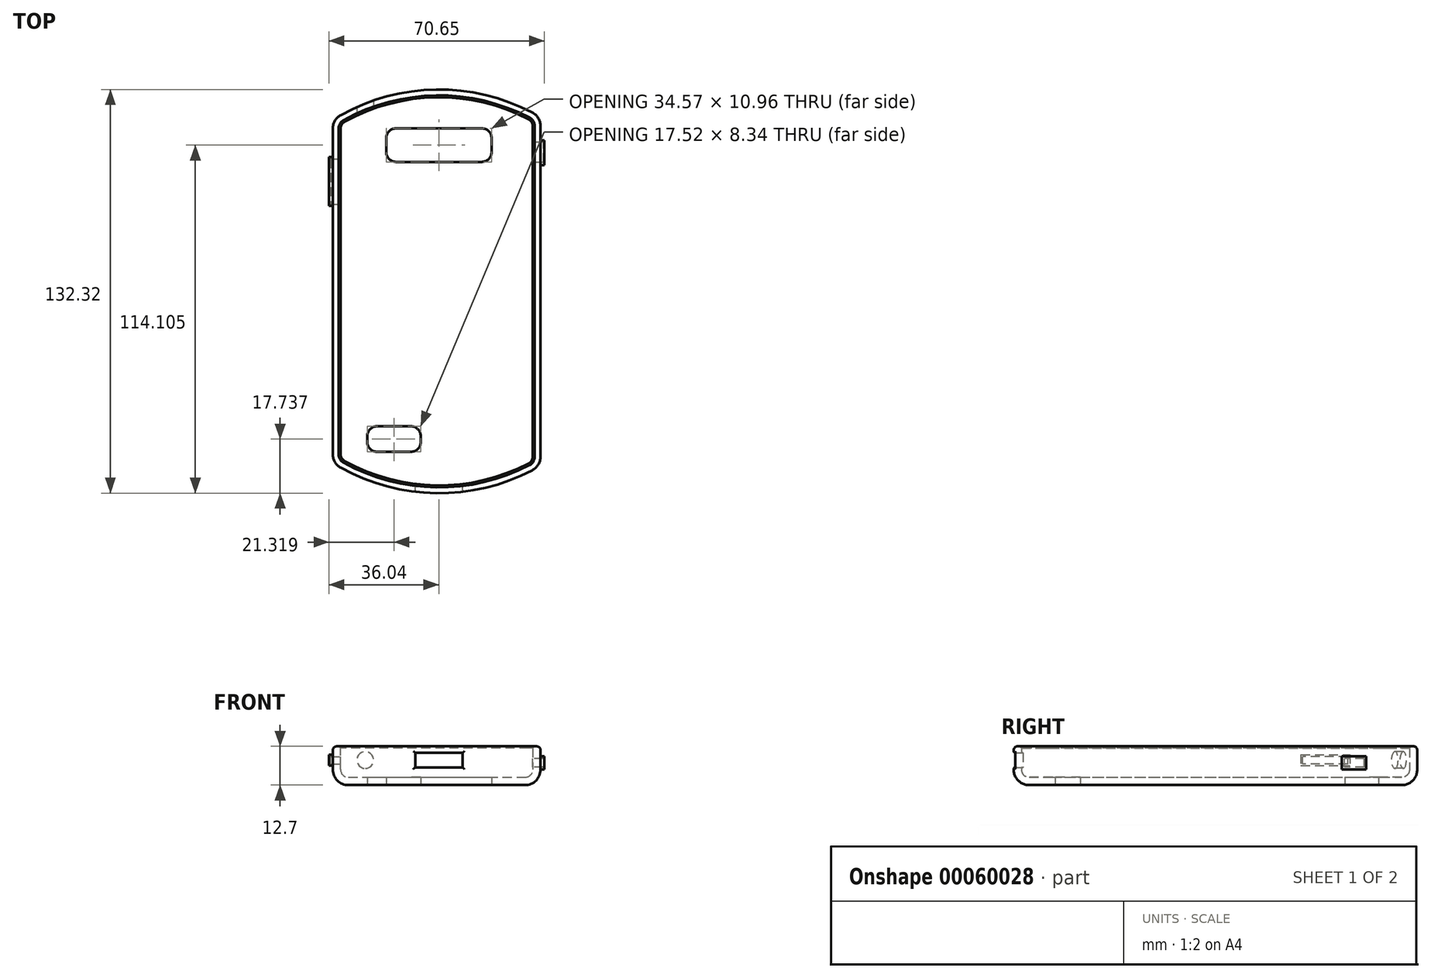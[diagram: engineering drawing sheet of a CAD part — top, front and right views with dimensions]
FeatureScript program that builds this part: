
annotation { "Feature Type Name" : "Feature", "Feature Type Description" : "" }
export const myFeature = defineFeature(function(context is Context, id is Id, definition is map)
    precondition{}
    {
        {
            var Q0;
            Q0=qCreatedBy(makeId("Top.planeOp"),FACE);
            var sketch = newSketch(context, id + "F0", { "sketchPlane" : qUnion([Q0])});
            skLineSegment(sketch, "E0.rect.left", {"start": v(33.34, 57.15) * mm, "end": v(33.34, -57.15) * mm});
            skLineSegment(sketch, "E0.rect.right", {"start": v(-34.77, 56.29) * mm, "end": v(-34.77, -56.29) * mm});
            skPoint(sketch, "E0.rect.middle", {"position": v(0, 0) * mm});
            skArc(sketch, "E1", {"start": v(33.34, 57.15) * mm, "mid": v(-0.84, 66.16) * mm, "end": v(-34.77, 56.29) * mm});
            skArc(sketch, "E2", {"start": v(33.34, -57.15) * mm, "mid": v(-0.84, -66.16) * mm, "end": v(-34.77, -56.29) * mm});
            skArc(sketch, "E3.0", {"start": v(36.51, 58.95) * mm, "mid": v(-0.85, 69.33) * mm, "end": v(-37.95, 58.03) * mm});
            skLineSegment(sketch, "E3.1", {"start": v(36.51, 58.95) * mm, "end": v(36.51, -58.95) * mm});
            skArc(sketch, "E3.2", {"start": v(36.51, -58.95) * mm, "mid": v(-0.85, -69.33) * mm, "end": v(-37.95, -58.03) * mm});
            skLineSegment(sketch, "E3.3", {"start": v(-37.95, 58.03) * mm, "end": v(-37.95, -58.03) * mm});
            skSolve(sketch);
        }
        {
            var Q0;
            Q0=makeQuery(id+"F0.imprint","IMPRINT",FACE,{"disambiguationData":[TD([[makeQuery(id+"F0.imprint","IMPRINT",EDGE,{"derivedFrom":sQuery(id+"F0.wireOp",EDGE,"E0.rect.left")}),-1.0]])]});
            extrude(context, id + "F1", {"entities" : qUnion([Q0]), "depth" : 12.7 * mm});
        }
        {
            var Q0;
            Q0=makeQuery(id+"F1.opExtrude","SWEPT_EDGE",EDGE,{"disambiguationData":[OSD([sQuery(id+"F0.wireOp",EDGE,"E0.rect.left"),sQuery(id+"F0.wireOp",EDGE,"E2")])]});
            var Q1;
            Q1=makeQuery(id+"F1.opExtrude","CAP_EDGE",EDGE,{"disambiguationData":[OSD([sQuery(id+"F0.wireOp",EDGE,"E0.rect.left")])],"isStart":true});
            var Q2;
            Q2=makeQuery(id+"F1.opExtrude","CAP_EDGE",EDGE,{"disambiguationData":[OSD([sQuery(id+"F0.wireOp",EDGE,"E0.rect.right")])],"isStart":true});
            var Q3;
            Q3=makeQuery(id+"F1.opExtrude","CAP_EDGE",EDGE,{"disambiguationData":[OSD([sQuery(id+"F0.wireOp",EDGE,"E1")])],"isStart":true});
            var Q4;
            Q4=makeQuery(id+"F1.opExtrude","SWEPT_EDGE",EDGE,{"disambiguationData":[OSD([sQuery(id+"F0.wireOp",EDGE,"E0.rect.right"),sQuery(id+"F0.wireOp",EDGE,"E1")])]});
            var Q5;
            Q5=makeQuery(id+"F1.opExtrude","SWEPT_EDGE",EDGE,{"disambiguationData":[OSD([sQuery(id+"F0.wireOp",EDGE,"E0.rect.left"),sQuery(id+"F0.wireOp",EDGE,"E1")])]});
            var Q6;
            Q6=makeQuery(id+"F1.opExtrude","CAP_EDGE",EDGE,{"disambiguationData":[OSD([sQuery(id+"F0.wireOp",EDGE,"E2")])],"isStart":true});
            var Q7;
            Q7=makeQuery(id+"F1.opExtrude","SWEPT_EDGE",EDGE,{"disambiguationData":[OSD([sQuery(id+"F0.wireOp",EDGE,"E0.rect.right"),sQuery(id+"F0.wireOp",EDGE,"E2")])]});
            fillet(context, id + "F2", {"entities" : qUnion([Q0, Q1, Q2, Q3, Q4, Q5, Q6, Q7]), "radius" : 5.08 * mm, "tangentPropagation" : true, "allowEdgeOverflow" : false});
        }
        {
            var Q0;
            Q0=makeQuery(id+"F1.opExtrude","CAP_FACE",FACE,{"disambiguationData":[OSD([sQuery(id+"F0.wireOp",EDGE,"E0.rect.left"),sQuery(id+"F0.wireOp",EDGE,"E0.rect.right"),sQuery(id+"F0.wireOp",EDGE,"E1"),sQuery(id+"F0.wireOp",EDGE,"E2")])],"isStart":false});
            shell(context, id + "F3", {"entities" : qUnion([Q0]), "thickness" : 2.54 * mm});
        }
        {
            var Q0;
            {var subQ0=sQuery(id+"F0.wireOp",EDGE,"E1");Q0=makeQuery(id+"F3.opShell","OFFSET_EDGE",EDGE,{"disambiguationData":[OSD([subQ0]),TDD([makeQuery(id+"F1.opExtrude","CAP_EDGE",EDGE,{"disambiguationData":[OSD([subQ0])],"isStart":false})])]});}
            var Q1;
            {var subQ0=sQuery(id+"F0.wireOp",EDGE,"E0.rect.left");Q1=makeQuery(id+"F3.opShell","OFFSET_EDGE",EDGE,{"disambiguationData":[OSD([subQ0]),TDD([makeQuery(id+"F1.opExtrude","CAP_EDGE",EDGE,{"disambiguationData":[OSD([subQ0])],"isStart":false})])]});}
            var Q2;
            {var subQ0=sQuery(id+"F0.wireOp",EDGE,"E2");Q2=makeQuery(id+"F3.opShell","OFFSET_EDGE",EDGE,{"disambiguationData":[OSD([subQ0]),TDD([makeQuery(id+"F1.opExtrude","CAP_EDGE",EDGE,{"disambiguationData":[OSD([subQ0])],"isStart":false})])]});}
            var Q3;
            {var subQ0=sQuery(id+"F0.wireOp",EDGE,"E0.rect.right");Q3=makeQuery(id+"F3.opShell","OFFSET_EDGE",EDGE,{"disambiguationData":[OSD([subQ0]),TDD([makeQuery(id+"F1.opExtrude","CAP_EDGE",EDGE,{"disambiguationData":[OSD([subQ0])],"isStart":false})])]});}
            var Q4;
            {var subQ0=sQuery(id+"F0.wireOp",EDGE,"E1");var subQ1=sQuery(id+"F0.wireOp",EDGE,"E0.rect.right");Q4=makeQuery(id+"F3.opShell","OFFSET_EDGE",EDGE,{"disambiguationData":[OSD([subQ1,subQ0]),TDD([makeQuery(id+"F2.opFillet","BLEND_EDGE",EDGE,{"blendedFrom":[makeQuery(id+"F1.opExtrude","SWEPT_EDGE",EDGE,{"disambiguationData":[OSD([subQ1,subQ0])]}),makeQuery(id+"F1.opExtrude","SWEPT_FACE",FACE,{"disambiguationData":[OSD([subQ0])]})],"blendedInto":[makeQuery(id+"F1.opExtrude","SWEPT_FACE",FACE,{"disambiguationData":[OSD([subQ0])]})]})])]});}
            var Q5;
            {var subQ0=sQuery(id+"F0.wireOp",EDGE,"E2");var subQ1=sQuery(id+"F0.wireOp",EDGE,"E1");var subQ2=sQuery(id+"F0.wireOp",EDGE,"E0.rect.right");var subQ3=sQuery(id+"F0.wireOp",EDGE,"E0.rect.left");Q5=makeQuery(id+"F3.opShell","OFFSET_EDGE",EDGE,{"disambiguationData":[OSD([subQ3,subQ2,subQ1,subQ0]),TDD([makeQuery(id+"F2.opFillet","BLEND_EDGE",EDGE,{"blendedFrom":[makeQuery(id+"F1.opExtrude","SWEPT_EDGE",EDGE,{"disambiguationData":[OSD([subQ3,subQ1])]}),makeQuery(id+"F1.opExtrude","CAP_FACE",FACE,{"disambiguationData":[OSD([subQ3,subQ2,subQ1,subQ0])],"isStart":false})],"blendedInto":[makeQuery(id+"F1.opExtrude","CAP_FACE",FACE,{"disambiguationData":[OSD([subQ3,subQ2,subQ1,subQ0])],"isStart":false})]})])]});}
            var Q6;
            {var subQ0=sQuery(id+"F0.wireOp",EDGE,"E2");var subQ1=sQuery(id+"F0.wireOp",EDGE,"E1");var subQ2=sQuery(id+"F0.wireOp",EDGE,"E0.rect.right");var subQ3=sQuery(id+"F0.wireOp",EDGE,"E0.rect.left");Q6=makeQuery(id+"F3.opShell","OFFSET_EDGE",EDGE,{"disambiguationData":[OSD([subQ3,subQ2,subQ1,subQ0]),TDD([makeQuery(id+"F2.opFillet","BLEND_EDGE",EDGE,{"blendedFrom":[makeQuery(id+"F1.opExtrude","SWEPT_EDGE",EDGE,{"disambiguationData":[OSD([subQ3,subQ0])]}),makeQuery(id+"F1.opExtrude","CAP_FACE",FACE,{"disambiguationData":[OSD([subQ3,subQ2,subQ1,subQ0])],"isStart":false})],"blendedInto":[makeQuery(id+"F1.opExtrude","CAP_FACE",FACE,{"disambiguationData":[OSD([subQ3,subQ2,subQ1,subQ0])],"isStart":false})]})])]});}
            var Q7;
            {var subQ0=sQuery(id+"F0.wireOp",EDGE,"E2");var subQ1=sQuery(id+"F0.wireOp",EDGE,"E1");var subQ2=sQuery(id+"F0.wireOp",EDGE,"E0.rect.right");var subQ3=sQuery(id+"F0.wireOp",EDGE,"E0.rect.left");Q7=makeQuery(id+"F3.opShell","OFFSET_EDGE",EDGE,{"disambiguationData":[OSD([subQ3,subQ2,subQ1,subQ0]),TDD([makeQuery(id+"F2.opFillet","BLEND_EDGE",EDGE,{"blendedFrom":[makeQuery(id+"F1.opExtrude","SWEPT_EDGE",EDGE,{"disambiguationData":[OSD([subQ2,subQ0])]}),makeQuery(id+"F1.opExtrude","CAP_FACE",FACE,{"disambiguationData":[OSD([subQ3,subQ2,subQ1,subQ0])],"isStart":false})],"blendedInto":[makeQuery(id+"F1.opExtrude","CAP_FACE",FACE,{"disambiguationData":[OSD([subQ3,subQ2,subQ1,subQ0])],"isStart":false})]})])]});}
            chamfer(context, id + "F4", {"entities" : qUnion([Q0, Q1, Q2, Q3, Q4, Q5, Q6, Q7]), "width" : 0.64 * mm, "tangentPropagation" : true});
        }
        {
            var Q0;
            Q0=makeQuery(id+"F1.opExtrude","CAP_EDGE",EDGE,{"disambiguationData":[OSD([sQuery(id+"F0.wireOp",EDGE,"E0.rect.left")])],"isStart":false});
            var Q1;
            {var subQ0=sQuery(id+"F0.wireOp",EDGE,"E2");var subQ1=sQuery(id+"F0.wireOp",EDGE,"E0.rect.left");Q1=makeQuery(id+"F2.opFillet","BLEND_EDGE",EDGE,{"blendedFrom":[makeQuery(id+"F1.opExtrude","SWEPT_EDGE",EDGE,{"disambiguationData":[OSD([subQ1,subQ0])]}),makeQuery(id+"F1.opExtrude","CAP_FACE",FACE,{"disambiguationData":[OSD([subQ1,sQuery(id+"F0.wireOp",EDGE,"E0.rect.right"),sQuery(id+"F0.wireOp",EDGE,"E1"),subQ0])],"isStart":false})],"blendedInto":[makeQuery(id+"F1.opExtrude","CAP_FACE",FACE,{"disambiguationData":[OSD([subQ1,sQuery(id+"F0.wireOp",EDGE,"E0.rect.right"),sQuery(id+"F0.wireOp",EDGE,"E1"),subQ0])],"isStart":false})]});}
            var Q2;
            Q2=makeQuery(id+"F1.opExtrude","CAP_EDGE",EDGE,{"disambiguationData":[OSD([sQuery(id+"F0.wireOp",EDGE,"E2")])],"isStart":false});
            var Q3;
            {var subQ0=sQuery(id+"F0.wireOp",EDGE,"E2");var subQ1=sQuery(id+"F0.wireOp",EDGE,"E0.rect.right");Q3=makeQuery(id+"F2.opFillet","BLEND_EDGE",EDGE,{"blendedFrom":[makeQuery(id+"F1.opExtrude","SWEPT_EDGE",EDGE,{"disambiguationData":[OSD([subQ1,subQ0])]}),makeQuery(id+"F1.opExtrude","CAP_FACE",FACE,{"disambiguationData":[OSD([sQuery(id+"F0.wireOp",EDGE,"E0.rect.left"),subQ1,sQuery(id+"F0.wireOp",EDGE,"E1"),subQ0])],"isStart":false})],"blendedInto":[makeQuery(id+"F1.opExtrude","CAP_FACE",FACE,{"disambiguationData":[OSD([sQuery(id+"F0.wireOp",EDGE,"E0.rect.left"),subQ1,sQuery(id+"F0.wireOp",EDGE,"E1"),subQ0])],"isStart":false})]});}
            var Q4;
            Q4=makeQuery(id+"F1.opExtrude","CAP_EDGE",EDGE,{"disambiguationData":[OSD([sQuery(id+"F0.wireOp",EDGE,"E0.rect.right")])],"isStart":false});
            var Q5;
            {var subQ0=sQuery(id+"F0.wireOp",EDGE,"E1");var subQ1=sQuery(id+"F0.wireOp",EDGE,"E0.rect.right");Q5=makeQuery(id+"F2.opFillet","BLEND_EDGE",EDGE,{"blendedFrom":[makeQuery(id+"F1.opExtrude","SWEPT_EDGE",EDGE,{"disambiguationData":[OSD([subQ1,subQ0])]}),makeQuery(id+"F1.opExtrude","CAP_FACE",FACE,{"disambiguationData":[OSD([sQuery(id+"F0.wireOp",EDGE,"E0.rect.left"),subQ1,subQ0,sQuery(id+"F0.wireOp",EDGE,"E2")])],"isStart":false})],"blendedInto":[makeQuery(id+"F1.opExtrude","CAP_FACE",FACE,{"disambiguationData":[OSD([sQuery(id+"F0.wireOp",EDGE,"E0.rect.left"),subQ1,subQ0,sQuery(id+"F0.wireOp",EDGE,"E2")])],"isStart":false})]});}
            var Q6;
            Q6=makeQuery(id+"F1.opExtrude","CAP_EDGE",EDGE,{"disambiguationData":[OSD([sQuery(id+"F0.wireOp",EDGE,"E1")])],"isStart":false});
            var Q7;
            {var subQ0=sQuery(id+"F0.wireOp",EDGE,"E1");var subQ1=sQuery(id+"F0.wireOp",EDGE,"E0.rect.left");Q7=makeQuery(id+"F2.opFillet","BLEND_EDGE",EDGE,{"blendedFrom":[makeQuery(id+"F1.opExtrude","SWEPT_EDGE",EDGE,{"disambiguationData":[OSD([subQ1,subQ0])]}),makeQuery(id+"F1.opExtrude","CAP_FACE",FACE,{"disambiguationData":[OSD([subQ1,sQuery(id+"F0.wireOp",EDGE,"E0.rect.right"),subQ0,sQuery(id+"F0.wireOp",EDGE,"E2")])],"isStart":false})],"blendedInto":[makeQuery(id+"F1.opExtrude","CAP_FACE",FACE,{"disambiguationData":[OSD([subQ1,sQuery(id+"F0.wireOp",EDGE,"E0.rect.right"),subQ0,sQuery(id+"F0.wireOp",EDGE,"E2")])],"isStart":false})]});}
            fillet(context, id + "F5", {"entities" : qUnion([Q0, Q1, Q2, Q3, Q4, Q5, Q6, Q7]), "radius" : 1.27 * mm, "tangentPropagation" : true, "allowEdgeOverflow" : false});
        }
        {
            var Q0;
            Q0=qCreatedBy(makeId("Front.planeOp"),FACE);
            var sketch = newSketch(context, id + "F6", { "sketchPlane" : qUnion([Q0])});
            skLineSegment(sketch, "E4.rect.bottom", {"start": v(7.75, 5.8) * mm, "end": v(-7.75, 5.8) * mm});
            skLineSegment(sketch, "E4.rect.top", {"start": v(7.75, 10.58) * mm, "end": v(-7.75, 10.58) * mm});
            skLineSegment(sketch, "E4.rect.left", {"start": v(7.75, 5.8) * mm, "end": v(7.75, 10.58) * mm});
            skLineSegment(sketch, "E4.rect.right", {"start": v(-7.75, 5.8) * mm, "end": v(-7.75, 10.58) * mm});
            skPoint(sketch, "E4.rect.middle", {"position": v(0, 8.2) * mm});
            skSolve(sketch);
        }
        {
            var Q0;
            Q0 = qSketchRegion(id + "F6", true);
            extrude(context, id + "F7", {"entities" : qUnion([Q0]), "operationType" : NewBodyOperationType.REMOVE, "endBound" : BoundingType.THROUGH_ALL, "depth" : 25.4 * mm});
        }
        {
            var Q0;
            Q0=makeQuery(id+"F7.boolean.opBoolean","INTERSECT",EDGE,{"derivedFrom":[makeQuery(id+"F1.opExtrude","SWEPT_FACE",FACE,{"disambiguationData":[OSD([sQuery(id+"F0.wireOp",EDGE,"E2")])]}),makeQuery(id+"F7.opExtrude","SWEPT_FACE",FACE,{"disambiguationData":[OSD([sQuery(id+"F6.wireOp",EDGE,"E4.rect.right")])]})]});
            var Q1;
            Q1=makeQuery(id+"F7.boolean.opBoolean","INTERSECT",EDGE,{"derivedFrom":[makeQuery(id+"F1.opExtrude","SWEPT_FACE",FACE,{"disambiguationData":[OSD([sQuery(id+"F0.wireOp",EDGE,"E2")])]}),makeQuery(id+"F7.opExtrude","SWEPT_FACE",FACE,{"disambiguationData":[OSD([sQuery(id+"F6.wireOp",EDGE,"E4.rect.left")])]})]});
            var Q2;
            Q2=makeQuery(id+"F7.boolean.opBoolean","INTERSECT",EDGE,{"derivedFrom":[makeQuery(id+"F1.opExtrude","SWEPT_FACE",FACE,{"disambiguationData":[OSD([sQuery(id+"F0.wireOp",EDGE,"E2")])]}),makeQuery(id+"F7.opExtrude","SWEPT_FACE",FACE,{"disambiguationData":[OSD([sQuery(id+"F6.wireOp",EDGE,"E4.rect.bottom")])]})]});
            var Q3;
            Q3=makeQuery(id+"F7.boolean.opBoolean","INTERSECT",EDGE,{"derivedFrom":[makeQuery(id+"F1.opExtrude","SWEPT_FACE",FACE,{"disambiguationData":[OSD([sQuery(id+"F0.wireOp",EDGE,"E2")])]}),makeQuery(id+"F7.opExtrude","SWEPT_FACE",FACE,{"disambiguationData":[OSD([sQuery(id+"F6.wireOp",EDGE,"E4.rect.top")])]})]});
            fillet(context, id + "F8", {"entities" : qUnion([Q0, Q1, Q2, Q3]), "radius" : 0.5 * mm, "tangentPropagation" : true, "allowEdgeOverflow" : false});
        }
        {
            var Q0;
            Q0=makeQuery(id+"F1.opExtrude","SWEPT_FACE",FACE,{"disambiguationData":[OSD([sQuery(id+"F0.wireOp",EDGE,"E0.rect.left")])]});
            var sketch = newSketch(context, id + "F9", { "sketchPlane" : qUnion([Q0])});
            skLineSegment(sketch, "E5.rect.bottom", {"start": v(49.47, 5.08) * mm, "end": v(41.42, 5.08) * mm});
            skLineSegment(sketch, "E5.rect.top", {"start": v(49.47, 9.39) * mm, "end": v(41.42, 9.39) * mm});
            skLineSegment(sketch, "E5.rect.left", {"start": v(49.47, 5.08) * mm, "end": v(49.47, 9.39) * mm});
            skLineSegment(sketch, "E5.rect.right", {"start": v(41.42, 5.08) * mm, "end": v(41.42, 9.39) * mm});
            skPoint(sketch, "E5.rect.middle", {"position": v(45.44, 7.23) * mm});
            skSolve(sketch);
        }
        {
            var Q0;
            Q0 = qSketchRegion(id + "F9", true);
            extrude(context, id + "F10", {"entities" : qUnion([Q0]), "operationType" : NewBodyOperationType.ADD, "depth" : 1.27 * mm});
        }
        {
            var Q0;
            Q0=qCreatedBy(makeId("Front.planeOp"),FACE);
            var sketch = newSketch(context, id + "F11", { "sketchPlane" : qUnion([Q0])});
            skCircle(sketch, "E6", {"center": v(-24.14, 8.2) * mm, "radius": 2.74 * mm});
            skSolve(sketch);
        }
        {
            var Q0;
            Q0 = qSketchRegion(id + "F11", true);
            extrude(context, id + "F12", {"entities" : qUnion([Q0]), "operationType" : NewBodyOperationType.REMOVE, "endBound" : BoundingType.THROUGH_ALL, "oppositeDirection" : true, "depth" : 25.4 * mm});
        }
        {
            var Q0;
            Q0=makeQuery(id+"F1.opExtrude","SWEPT_FACE",FACE,{"disambiguationData":[OSD([sQuery(id+"F0.wireOp",EDGE,"E0.rect.right")])]});
            var sketch = newSketch(context, id + "F13", { "sketchPlane" : qUnion([Q0])});
            skLineSegment(sketch, "E7.rect.bottom", {"start": v(-28.01, 9.98) * mm, "end": v(-44.1, 9.98) * mm});
            skLineSegment(sketch, "E7.rect.top", {"start": v(-28.01, 6.4) * mm, "end": v(-44.1, 6.4) * mm});
            skLineSegment(sketch, "E7.rect.left", {"start": v(-28.01, 9.98) * mm, "end": v(-28.01, 6.4) * mm});
            skLineSegment(sketch, "E7.rect.right", {"start": v(-44.1, 9.98) * mm, "end": v(-44.1, 6.4) * mm});
            skPoint(sketch, "E7.rect.middle", {"position": v(-36.06, 8.2) * mm});
            skSolve(sketch);
        }
        {
            var Q0;
            Q0 = qSketchRegion(id + "F13", true);
            extrude(context, id + "F14", {"entities" : qUnion([Q0]), "operationType" : NewBodyOperationType.ADD, "depth" : 1.27 * mm});
        }
        {
            var Q0;
            Q0=makeQuery(id+"F1.opExtrude","CAP_FACE",FACE,{"disambiguationData":[OSD([sQuery(id+"F0.wireOp",EDGE,"E0.rect.left"),sQuery(id+"F0.wireOp",EDGE,"E0.rect.right"),sQuery(id+"F0.wireOp",EDGE,"E1"),sQuery(id+"F0.wireOp",EDGE,"E2")])],"isStart":true});
            var sketch = newSketch(context, id + "F15", { "sketchPlane" : qUnion([Q0])});
            skLineSegment(sketch, "E8.rect.bottom", {"start": v(14.1, -53.43) * mm, "end": v(-14.1, -53.43) * mm});
            skLineSegment(sketch, "E8.rect.top", {"start": v(14.1, -42.46) * mm, "end": v(-14.1, -42.46) * mm});
            skLineSegment(sketch, "E8.rect.left", {"start": v(17.28, -50.25) * mm, "end": v(17.28, -45.64) * mm});
            skLineSegment(sketch, "E8.rect.right", {"start": v(-17.28, -50.25) * mm, "end": v(-17.28, -45.64) * mm});
            skPoint(sketch, "E8.rect.middle", {"position": v(0, -47.94) * mm});
            skPoint(sketch, "E9.visualSharp", {"position": v(-17.28, -42.46) * mm});
            skArc(sketch, "E9.filletArc", {"start": v(-14.1, -42.46) * mm, "mid": v(-16.35, -43.4) * mm, "end": v(-17.28, -45.64) * mm});
            skPoint(sketch, "E10.visualSharp", {"position": v(17.28, -42.46) * mm});
            skArc(sketch, "E10.filletArc", {"start": v(17.28, -45.64) * mm, "mid": v(16.35, -43.4) * mm, "end": v(14.1, -42.46) * mm});
            skPoint(sketch, "E11.visualSharp", {"position": v(17.28, -53.43) * mm});
            skArc(sketch, "E11.filletArc", {"start": v(14.1, -53.43) * mm, "mid": v(16.35, -52.5) * mm, "end": v(17.28, -50.25) * mm});
            skPoint(sketch, "E12.visualSharp", {"position": v(-17.28, -53.43) * mm});
            skArc(sketch, "E12.filletArc", {"start": v(-17.28, -50.25) * mm, "mid": v(-16.35, -52.5) * mm, "end": v(-14.1, -53.43) * mm});
            skSolve(sketch);
        }
        {
            var Q0;
            Q0 = qSketchRegion(id + "F15", true);
            extrude(context, id + "F16", {"entities" : qUnion([Q0]), "operationType" : NewBodyOperationType.REMOVE, "endBound" : BoundingType.THROUGH_ALL, "oppositeDirection" : true, "depth" : 25.4 * mm});
        }
        {
            var Q0;
            Q0=makeQuery(id+"F1.opExtrude","CAP_FACE",FACE,{"disambiguationData":[OSD([sQuery(id+"F0.wireOp",EDGE,"E0.rect.left"),sQuery(id+"F0.wireOp",EDGE,"E0.rect.right"),sQuery(id+"F0.wireOp",EDGE,"E1"),sQuery(id+"F0.wireOp",EDGE,"E2")])],"isStart":true});
            var sketch = newSketch(context, id + "F17", { "sketchPlane" : qUnion([Q0])});
            skLineSegment(sketch, "E13.rect.bottom", {"start": v(-9.13, 44.25) * mm, "end": v(-20.3, 44.25) * mm});
            skLineSegment(sketch, "E13.rect.top", {"start": v(-9.13, 52.6) * mm, "end": v(-20.3, 52.6) * mm});
            skLineSegment(sketch, "E13.rect.left", {"start": v(-5.96, 47.43) * mm, "end": v(-5.96, 49.42) * mm});
            skLineSegment(sketch, "E13.rect.right", {"start": v(-23.48, 47.43) * mm, "end": v(-23.48, 49.42) * mm});
            skPoint(sketch, "E13.rect.middle", {"position": v(-14.72, 48.42) * mm});
            skPoint(sketch, "E14.visualSharp", {"position": v(-23.48, 52.6) * mm});
            skArc(sketch, "E14.filletArc", {"start": v(-20.3, 52.6) * mm, "mid": v(-22.55, 51.67) * mm, "end": v(-23.48, 49.42) * mm});
            skPoint(sketch, "E15.visualSharp", {"position": v(-23.48, 44.25) * mm});
            skArc(sketch, "E15.filletArc", {"start": v(-23.48, 47.43) * mm, "mid": v(-22.55, 45.18) * mm, "end": v(-20.3, 44.25) * mm});
            skPoint(sketch, "E16.visualSharp", {"position": v(-5.96, 44.25) * mm});
            skArc(sketch, "E16.filletArc", {"start": v(-9.13, 44.25) * mm, "mid": v(-6.89, 45.18) * mm, "end": v(-5.96, 47.43) * mm});
            skPoint(sketch, "E17.visualSharp", {"position": v(-5.96, 52.6) * mm});
            skArc(sketch, "E17.filletArc", {"start": v(-5.96, 49.42) * mm, "mid": v(-6.89, 51.67) * mm, "end": v(-9.13, 52.6) * mm});
            skSolve(sketch);
        }
        {
            var Q0;
            Q0 = qSketchRegion(id + "F17", true);
            extrude(context, id + "F18", {"entities" : qUnion([Q0]), "operationType" : NewBodyOperationType.REMOVE, "endBound" : BoundingType.THROUGH_ALL, "oppositeDirection" : true, "depth" : 25.4 * mm});
        }
        {
            var Q0;
            Q0=qCreatedBy(makeId("Right.planeOp"),FACE);
            var sketch = newSketch(context, id + "F19", { "sketchPlane" : qUnion([Q0])});
            skLineSegment(sketch, "E18.rect.bottom", {"start": v(43.4, 6.9) * mm, "end": v(28.61, 6.9) * mm});
            skLineSegment(sketch, "E18.rect.top", {"start": v(43.4, 9.34) * mm, "end": v(28.61, 9.34) * mm});
            skLineSegment(sketch, "E18.rect.left", {"start": v(43.4, 6.9) * mm, "end": v(43.4, 9.34) * mm});
            skLineSegment(sketch, "E18.rect.right", {"start": v(28.61, 6.9) * mm, "end": v(28.61, 9.34) * mm});
            skPoint(sketch, "E18.rect.middle", {"position": v(36, 8.11) * mm});
            skSolve(sketch);
        }
        {
            var Q0;
            Q0=makeQuery(id+"F19.imprint","IMPRINT",FACE,{"disambiguationData":[TD([[makeQuery(id+"F19.imprint","IMPRINT",EDGE,{"derivedFrom":sQuery(id+"F19.wireOp",EDGE,"E18.rect.bottom")}),-1.0]])]});
            extrude(context, id + "F20", {"entities" : qUnion([Q0]), "operationType" : NewBodyOperationType.REMOVE, "oppositeDirection" : true, "depth" : 35.56 * mm});
        }
        {
            var Q0;
            Q0=qCreatedBy(makeId("Right.planeOp"),FACE);
            var sketch = newSketch(context, id + "F21", { "sketchPlane" : qUnion([Q0])});
            skLineSegment(sketch, "E19.rect.bottom", {"start": v(42.3, 8.7) * mm, "end": v(48.82, 8.7) * mm});
            skLineSegment(sketch, "E19.rect.top", {"start": v(42.3, 5.9) * mm, "end": v(48.82, 5.9) * mm});
            skLineSegment(sketch, "E19.rect.left", {"start": v(42.3, 8.7) * mm, "end": v(42.3, 5.9) * mm});
            skLineSegment(sketch, "E19.rect.right", {"start": v(48.82, 8.7) * mm, "end": v(48.82, 5.9) * mm});
            skPoint(sketch, "E19.rect.middle", {"position": v(45.56, 7.3) * mm});
            skSolve(sketch);
        }
        {
            var Q0;
            Q0 = qSketchRegion(id + "F21", true);
            extrude(context, id + "F22", {"entities" : qUnion([Q0]), "operationType" : NewBodyOperationType.REMOVE, "depth" : 34.3 * mm});
        }
    });
